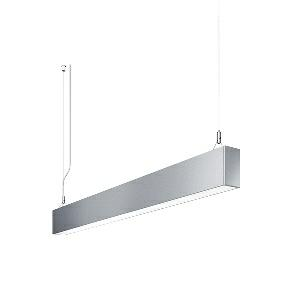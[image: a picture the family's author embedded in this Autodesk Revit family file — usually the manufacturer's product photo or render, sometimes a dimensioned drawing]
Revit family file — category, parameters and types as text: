
# Revit family: idoo_line_-_ilp_4000_830_d_00805739_c180
name_source: partatom
category: Lighting Fixtures
units: mm (PartAtom-declared; Revit-internal decimal feet)

## family parameters
Cut with Voids When Loaded = No
Host = Face
Light Source = No
Part Type = Normal
Room Calculation Point = No
Round Connector Dimension = Use Diameter
Shared = No

## types (1)
- IDOO.line - ILP 4000/830/D (1 x LED, 3750 lm, 3000K)
    Apparent Load = 29 VA
    Approval mark = CE
    CIE Flux Codes = 66 91 98 40 100
    Color Rendering = 80-89
    Color Temperature = 3000K
    Control Gear = Electronic ballast
    Default Elevation = 1800 mm
    Description = ILP 4000/830/D|Suspended luminaire|light source: LED|connected load: 220-240V, 50/60Hz|Power consumption: approx. 29 W|standby: approx. 0,15|luminous flux: 3750 lm|luminous efficacy: 129 lm/W|light distribution: Direct/indirect|direct ratio: approx. 40 %|colour temperature: Warm white, ca. 3000 K|color rendering index (CRI): >= 80|chromaticity tolerance:  3 SDCM|System of protection: IP 40|technology: Continuously dimmable|luminaire body|material: Sectional aluminium|colour: Silver|lamp cover: Acrylic (PMMA), Clear|mains lead: 2.00 m With free stranded wires|Fastening: Steel cable 0.3 - 0.7 m|glare control: Prism aperture|luminance(L65): <= 2700 cd/m|unified glare rating(4H 8H): <=  16|special features: DALI Load 1x, TouchDIM - dimming via standard switch, Flicker-free, Suitable as emergency lighting|
    Frequency = 50 Hz
    Height = 110 mm
    Lamp = 1 x LED
    Lamp Light Flux = 3750 lm
    Lamp count = 1
    Length = 1414 mm
    Luminous efficacy = 129 lm/W
    Manufacturer = Waldmann
    ModVariant = No
    Model = 00805739
    Mounting Place = Ceiling
    Mounting Type = Pendant
    Number of Poles = 1
    OnlyDefault = Yes
    Power Factor = 1
    Product Name = IDOO.line - ILP 4000/830/D
    Product group = Suspended luminaire
    ProductGroupID = 9
    Protection Class = Protection class I
    Protection Degree = IP 40
    RLX_Detail_Level = 1
    RLX_Emergency_Light_Flux = 0 lm
    RLX_Emergency_Type = 0
    RLX_Emergency_Type_DB = No
    RlxData = <blob elided: 21573 chars, md5=54a30d02>
    Socket = socket
    Standby Power = 0 W
    System Light Flux = 3750 lm
    System Power = 29 W
    Type Comments = Product without accessories
    Type Image = 113292000-00692525.jpg
    URL = http://relux.com
    VarID = ---
    Voltage = 230 V
    Voltage Range = 220-240 V
    Weight = 0.00 kg
    Width = 60 mm  [stored 0.19685 ft]

note: [stored X ft] marks values corroborated as IEEE doubles in the binary element streams (Revit-internal decimal feet)

## geometry (parser evidence)
native form markers: Blend x4, Sweep x12
no freeform markers — native parametric forms only
